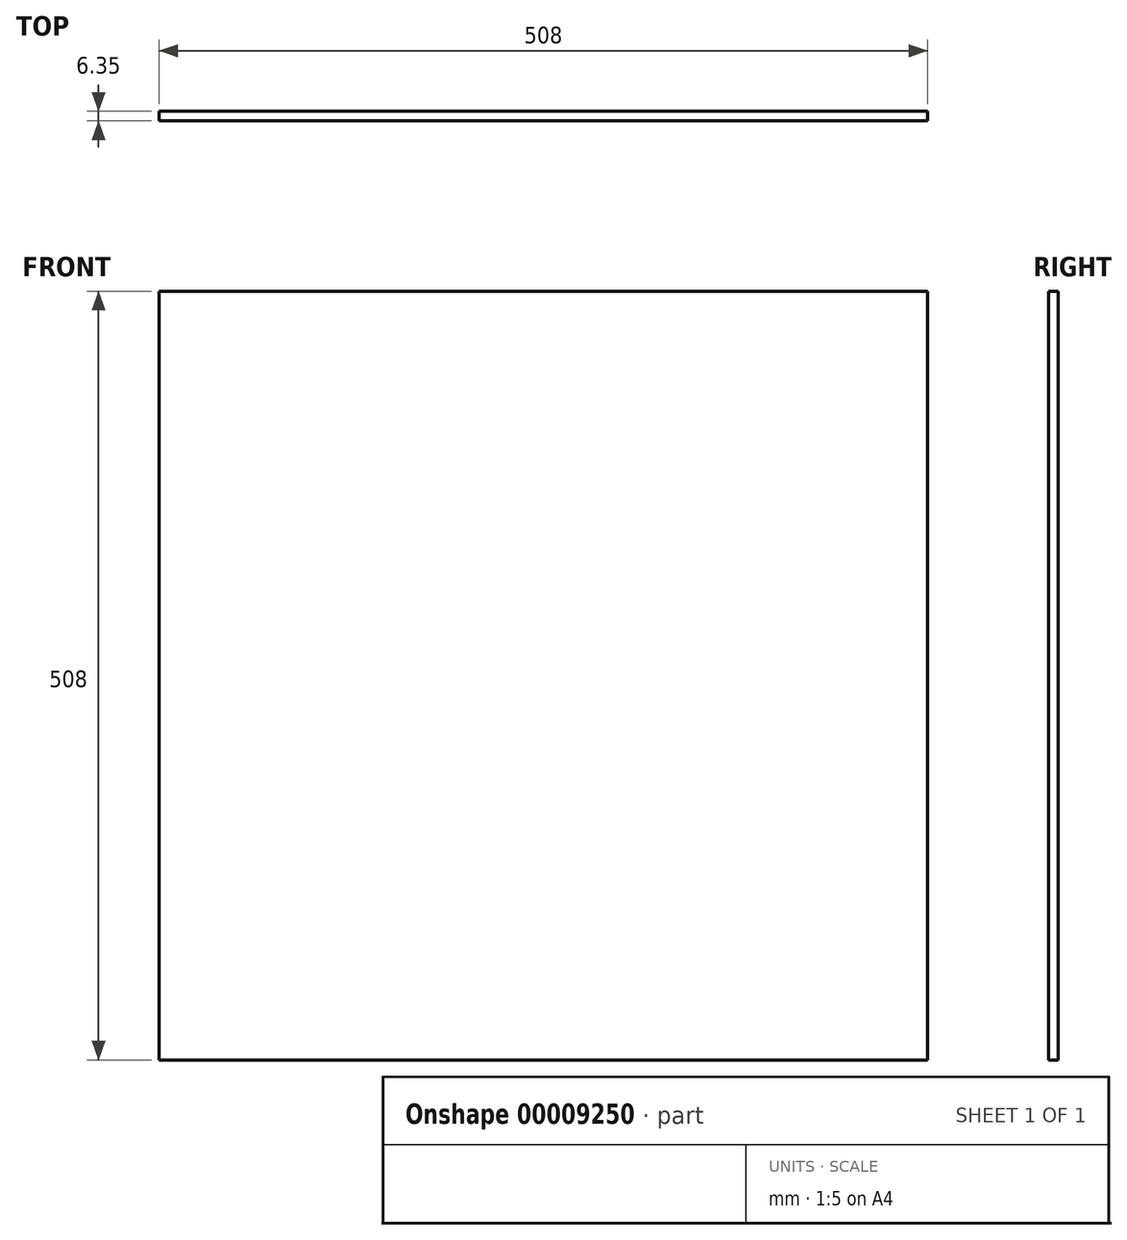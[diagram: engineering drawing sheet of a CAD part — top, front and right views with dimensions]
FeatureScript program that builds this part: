
annotation { "Feature Type Name" : "Feature", "Feature Type Description" : "" }
export const myFeature = defineFeature(function(context is Context, id is Id, definition is map)
    precondition{}
    {
        {
            var Q0;
            Q0=qCreatedBy(makeId("Front.planeOp"),FACE);
            var sketch = newSketch(context, id + "F0", { "sketchPlane" : qUnion([Q0])});
            skLineSegment(sketch, "E0.rect.bottom", {"start": v(254, 254) * mm, "end": v(-254, 254) * mm});
            skLineSegment(sketch, "E0.rect.top", {"start": v(254, -254) * mm, "end": v(-254, -254) * mm});
            skLineSegment(sketch, "E0.rect.left", {"start": v(254, 254) * mm, "end": v(254, -254) * mm});
            skLineSegment(sketch, "E0.rect.right", {"start": v(-254, 254) * mm, "end": v(-254, -254) * mm});
            skPoint(sketch, "E0.rect.middle", {"position": v(0, 0) * mm});
            skSolve(sketch);
        }
        {
            var Q0;
            Q0=makeQuery(id+"F0.imprint","IMPRINT",FACE,{"disambiguationData":[TD([[makeQuery(id+"F0.imprint","IMPRINT",EDGE,{"derivedFrom":sQuery(id+"F0.wireOp",EDGE,"E0.rect.bottom")}),1.0]])]});
            extrude(context, id + "F1", {"entities" : qUnion([Q0]), "depth" : 6.35 * mm});
        }
    });
